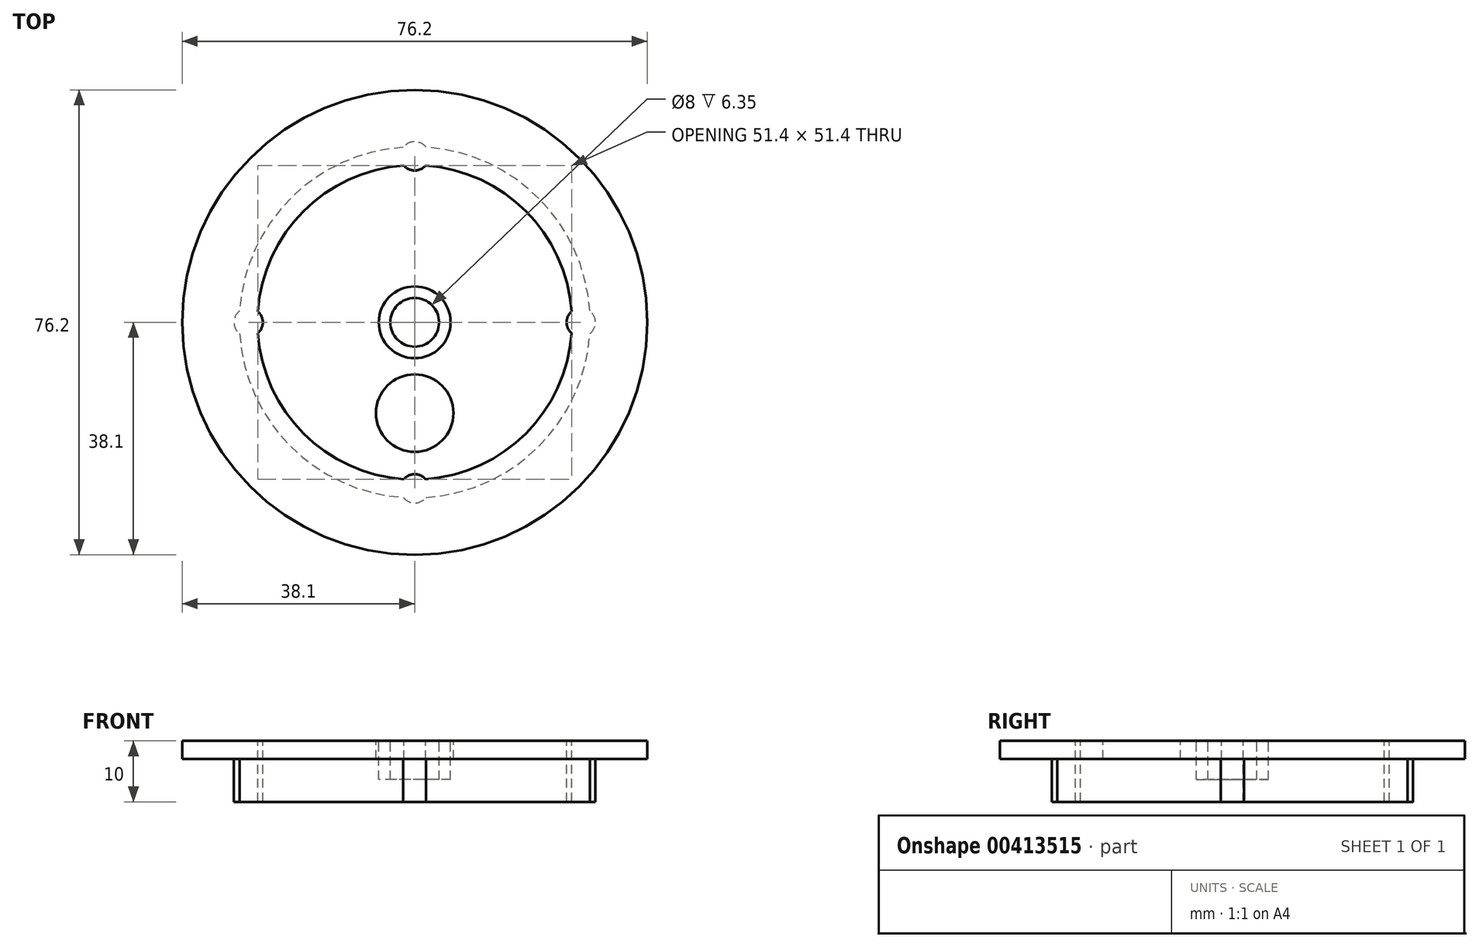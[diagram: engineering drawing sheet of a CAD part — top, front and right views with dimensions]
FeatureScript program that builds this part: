
annotation { "Feature Type Name" : "Feature", "Feature Type Description" : "" }
export const myFeature = defineFeature(function(context is Context, id is Id, definition is map)
    precondition{}
    {
        {
            var Q0;
            Q0=qCreatedBy(makeId("Top.planeOp"),FACE);
            var sketch = newSketch(context, id + "F0", { "sketchPlane" : qUnion([Q0])});
            skCircle(sketch, "E0", {"center": v(0, 0) * mm, "radius": 28.75 * mm});
            skCircle(sketch, "E1", {"center": v(0, 0) * mm, "radius": 25.76 * mm});
            skLineSegment(sketch, "E2", {"start": v(-14.03, 21.6) * mm, "end": v(-15.9, 23.95) * mm, "construction": true});
            skCircle(sketch, "E3", {"center": v(0, 0) * mm, "radius": 4 * mm});
            skCircle(sketch, "E4", {"center": v(0, 0) * mm, "radius": 38.1 * mm});
            skPoint(sketch, "E5", {"position": v(0, 14.88) * mm});
            skCircle(sketch, "E6", {"center": v(0, 14.88) * mm, "radius": 6.35 * mm});
            skCircle(sketch, "E7.MirrorC", {"center": v(0, -14.88) * mm, "radius": 6.35 * mm});
            skCircle(sketch, "E8.MirrorC", {"center": v(14.9, 0) * mm, "radius": 6.35 * mm});
            skCircle(sketch, "E9.MirrorC", {"center": v(-14.9, 0) * mm, "radius": 6.35 * mm});
            skCircle(sketch, "E10", {"center": v(0, 0) * mm, "radius": 5.88 * mm});
            skLineSegment(sketch, "E11", {"start": v(0, -25.76) * mm, "end": v(0, -28.75) * mm});
            skLineSegment(sketch, "E12", {"start": v(25.76, 0) * mm, "end": v(28.75, 0) * mm});
            skLineSegment(sketch, "E13", {"start": v(0, 25.76) * mm, "end": v(0, 28.75) * mm});
            skLineSegment(sketch, "E14", {"start": v(-25.76, 0) * mm, "end": v(-28.75, 0) * mm});
            skCircle(sketch, "E15", {"center": v(-27.26, 0) * mm, "radius": 2.36 * mm});
            skCircle(sketch, "E16", {"center": v(0, -27.26) * mm, "radius": 2.36 * mm});
            skCircle(sketch, "E17", {"center": v(0, 27.26) * mm, "radius": 2.36 * mm});
            skCircle(sketch, "E18", {"center": v(27.26, 0) * mm, "radius": 2.36 * mm});
            skSolve(sketch);
        }
        {
            var Q0;
            Q0=makeQuery(id+"F0.imprint","IMPRINT",FACE,{"disambiguationData":[TD([[makeQuery(id+"F0.imprint","IMPRINT",EDGE,{"derivedFrom":sQuery(id+"F0.wireOp",EDGE,"E0")}),-1.0]])]});
            var Q1;
            Q1=makeQuery(id+"F0.imprint","IMPRINT",FACE,{"disambiguationData":[TD([[makeQuery(id+"F0.imprint","IMPRINT",EDGE,{"derivedFrom":sQuery(id+"F0.wireOp",EDGE,"E0")}),1.0]])]});
            var Q2;
            Q2=makeQuery(id+"F0.imprint","IMPRINT",FACE,{"disambiguationData":[TD([[makeQuery(id+"F0.imprint","IMPRINT",EDGE,{"derivedFrom":sQuery(id+"F0.wireOp",EDGE,"E1")}),1.0]])]});
            extrude(context, id + "F1", {"entities" : qUnion([Q0, Q1, Q2]), "oppositeDirection" : true, "depth" : 10 * mm});
        }
        {
            var Q0;
            Q0=makeQuery(id+"F0.imprint","IMPRINT",FACE,{"disambiguationData":[TD([[makeQuery(id+"F0.imprint","IMPRINT",EDGE,{"derivedFrom":sQuery(id+"F0.wireOp",EDGE,"E4")}),1.0]])]});
            var Q1;
            Q1=makeQuery(id+"F0.imprint","IMPRINT",FACE,{"disambiguationData":[TD([[makeQuery(id+"F0.imprint","IMPRINT",EDGE,{"derivedFrom":sQuery(id+"F0.wireOp",EDGE,"E7.MirrorC")}),1.0]])]});
            extrude(context, id + "F2", {"entities" : qUnion([Q0, Q1]), "operationType" : NewBodyOperationType.ADD, "oppositeDirection" : true, "depth" : 3 * mm});
        }
        {
            var Q0;
            Q0=makeQuery(id+"F0.imprint","IMPRINT",FACE,{"disambiguationData":[TD([[makeQuery(id+"F0.imprint","IMPRINT",EDGE,{"derivedFrom":sQuery(id+"F0.wireOp",EDGE,"E3")}),-1.0]])]});
            extrude(context, id + "F3", {"entities" : qUnion([Q0]), "operationType" : NewBodyOperationType.ADD, "oppositeDirection" : true, "depth" : 6.35 * mm});
        }
    });
